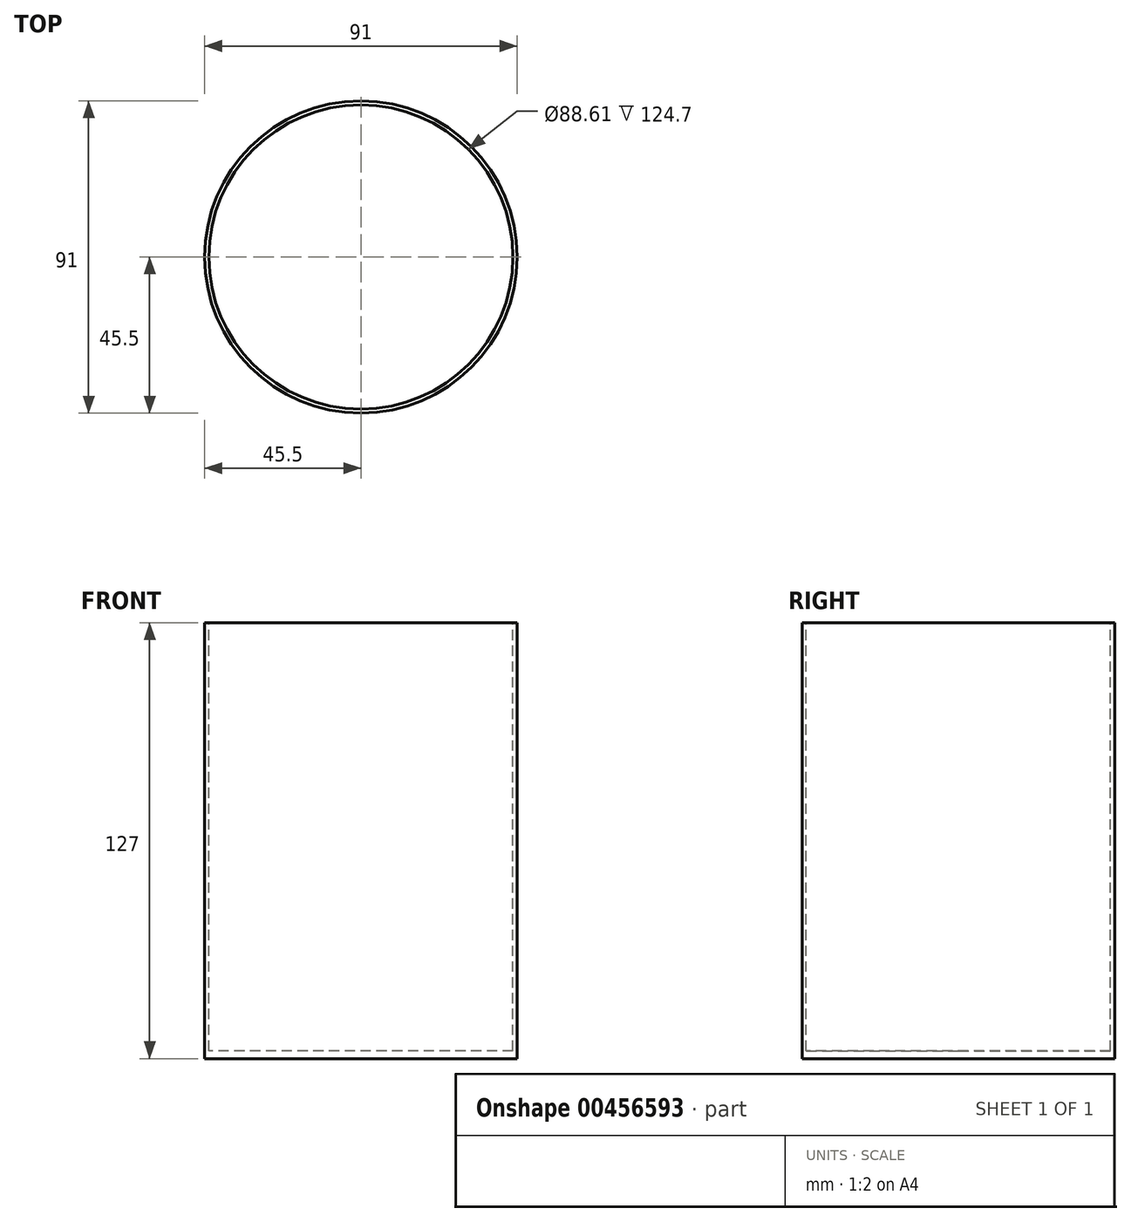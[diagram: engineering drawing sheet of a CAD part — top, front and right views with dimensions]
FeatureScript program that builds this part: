
annotation { "Feature Type Name" : "Feature", "Feature Type Description" : "" }
export const myFeature = defineFeature(function(context is Context, id is Id, definition is map)
    precondition{}
    {
        {
            var Q0;
            Q0=qCreatedBy(makeId("Top.planeOp"),FACE);
            var sketch = newSketch(context, id + "F0", { "sketchPlane" : qUnion([Q0])});
            skCircle(sketch, "E0", {"center": v(0, 0) * mm, "radius": 45.5 * mm});
            skSolve(sketch);
        }
        {
            var Q0;
            Q0 = qSketchRegion(id + "F0", true);
            extrude(context, id + "F1", {"entities" : qUnion([Q0]), "oppositeDirection" : true, "depth" : 127 * mm});
        }
        {
            var Q0;
            Q0=makeQuery(id+"F1.opExtrude","CAP_FACE",FACE,{"disambiguationData":[OSD([sQuery(id+"F0.wireOp",EDGE,"E0")])],"isStart":true});
            var sketch = newSketch(context, id + "F2", { "sketchPlane" : qUnion([Q0])});
            skCircle(sketch, "E1", {"center": v(0, 0) * mm, "radius": 44.3 * mm});
            skSolve(sketch);
        }
        {
            var Q0;
            Q0 = qSketchRegion(id + "F2", true);
            extrude(context, id + "F3", {"entities" : qUnion([Q0]), "operationType" : NewBodyOperationType.REMOVE, "oppositeDirection" : true, "depth" : 124.7 * mm});
        }
    });
